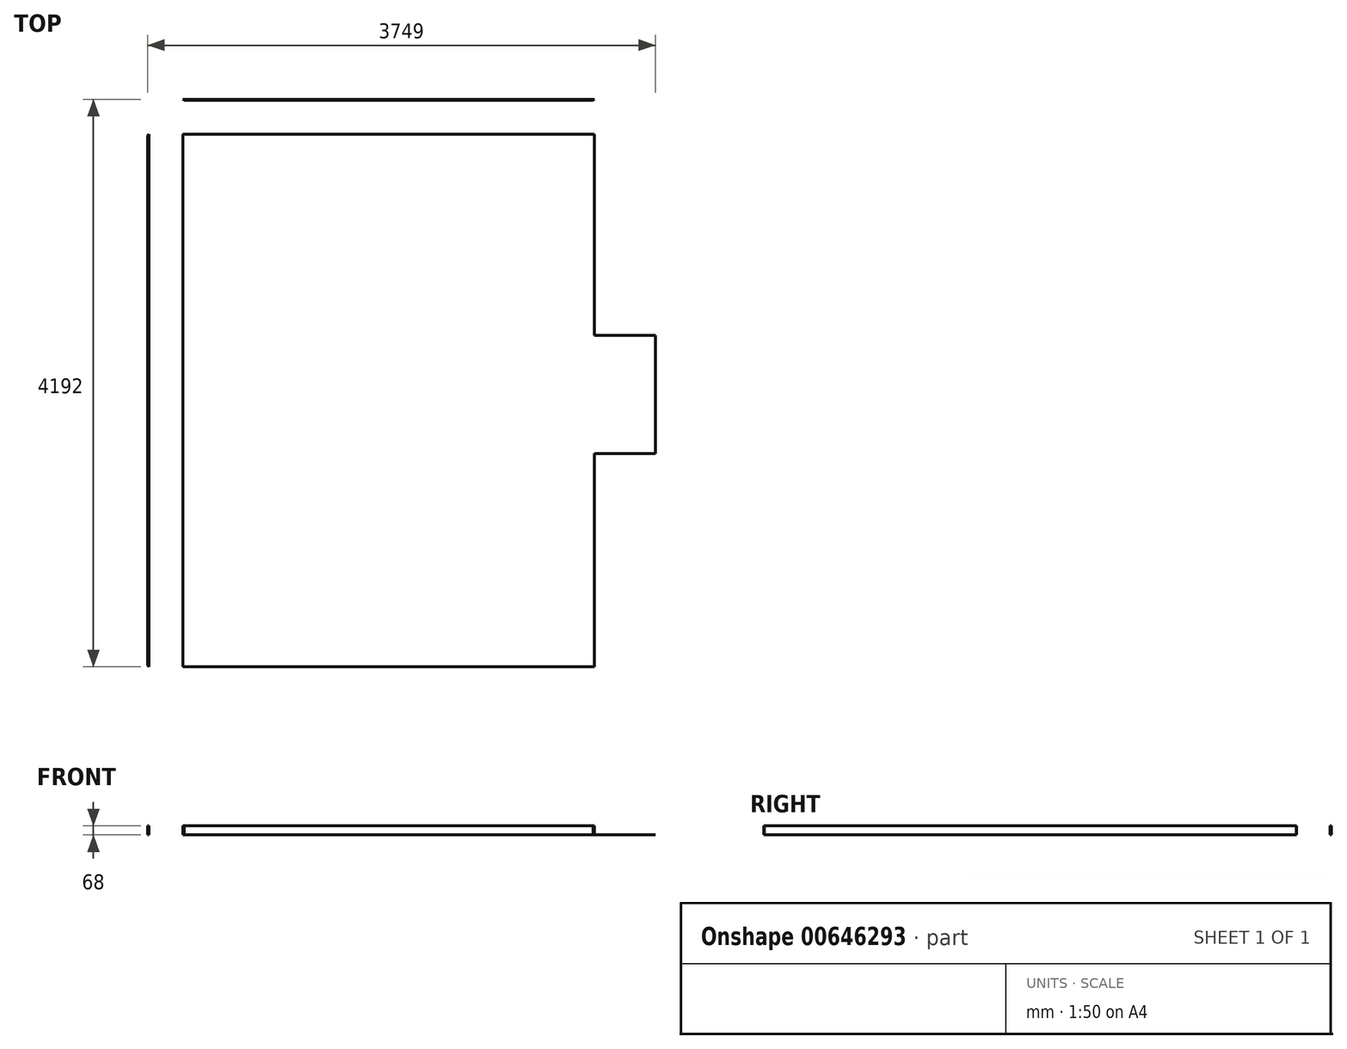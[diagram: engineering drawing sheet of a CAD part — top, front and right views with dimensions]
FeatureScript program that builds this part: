
annotation { "Feature Type Name" : "Feature", "Feature Type Description" : "" }
export const myFeature = defineFeature(function(context is Context, id is Id, definition is map)
    precondition{}
    {
        {
            var Q0;
            Q0=qCreatedBy(makeId("Top.planeOp"),FACE);
            var sketch = newSketch(context, id + "F0", { "sketchPlane" : qUnion([Q0])});
            skLineSegment(sketch, "E0", {"start": v(0, 0) * mm, "end": v(0, 3933) * mm});
            skLineSegment(sketch, "E1", {"start": v(0, 3933) * mm, "end": v(3040, 3933) * mm});
            skLineSegment(sketch, "E2", {"start": v(3040, 3933) * mm, "end": v(3040, 2448) * mm});
            skLineSegment(sketch, "E3", {"start": v(3040, 2448) * mm, "end": v(3490, 2448) * mm});
            skLineSegment(sketch, "E4", {"start": v(3490, 2448) * mm, "end": v(3490, 1573) * mm});
            skLineSegment(sketch, "E5", {"start": v(3490, 1573) * mm, "end": v(3040, 1573) * mm});
            skLineSegment(sketch, "E6", {"start": v(3040, 1573) * mm, "end": v(3040, 0) * mm});
            skLineSegment(sketch, "E7", {"start": v(3040, 0) * mm, "end": v(0, 0) * mm});
            skSolve(sketch);
        }
        {
            var Q0;
            Q0 = qSketchRegion(id + "F0", true);
            extrude(context, id + "F1", {"entities" : qUnion([Q0]), "oppositeDirection" : true, "depth" : 2 * mm, "offsetDistance" : 25 * mm});
        }
        {
            var Q0;
            Q0=qCreatedBy(makeId("Top.planeOp"),FACE);
            var sketch = newSketch(context, id + "F2", { "sketchPlane" : qUnion([Q0])});
            skLineSegment(sketch, "E8", {"start": v(-250, 0) * mm, "end": v(-250, 3933) * mm});
            skLineSegment(sketch, "E9", {"start": v(-250, 3933) * mm, "end": v(-259, 3924) * mm});
            skLineSegment(sketch, "E10", {"start": v(-259, 3924) * mm, "end": v(-259, 9) * mm});
            skLineSegment(sketch, "E11", {"start": v(-259, 9) * mm, "end": v(-250, 0) * mm});
            skSolve(sketch);
        }
        {
            var Q0;
            Q0 = qSketchRegion(id + "F2", true);
            extrude(context, id + "F3", {"entities" : qUnion([Q0]), "depth" : 66 * mm, "offsetDistance" : 25 * mm});
        }
        {
            var Q0;
            Q0=qCreatedBy(makeId("Top.planeOp"),FACE);
            var sketch = newSketch(context, id + "F4", { "sketchPlane" : qUnion([Q0])});
            skLineSegment(sketch, "E12", {"start": v(0, 4192) * mm, "end": v(9, 4183) * mm});
            skLineSegment(sketch, "E13", {"start": v(9, 4183) * mm, "end": v(3031, 4183) * mm});
            skLineSegment(sketch, "E14", {"start": v(3031, 4183) * mm, "end": v(3040, 4192) * mm});
            skLineSegment(sketch, "E15", {"start": v(3040, 4192) * mm, "end": v(0, 4192) * mm});
            skSolve(sketch);
        }
        {
            var Q0;
            Q0 = qSketchRegion(id + "F4", true);
            extrude(context, id + "F5", {"entities" : qUnion([Q0]), "depth" : 66 * mm, "offsetDistance" : 25 * mm});
        }
    });
